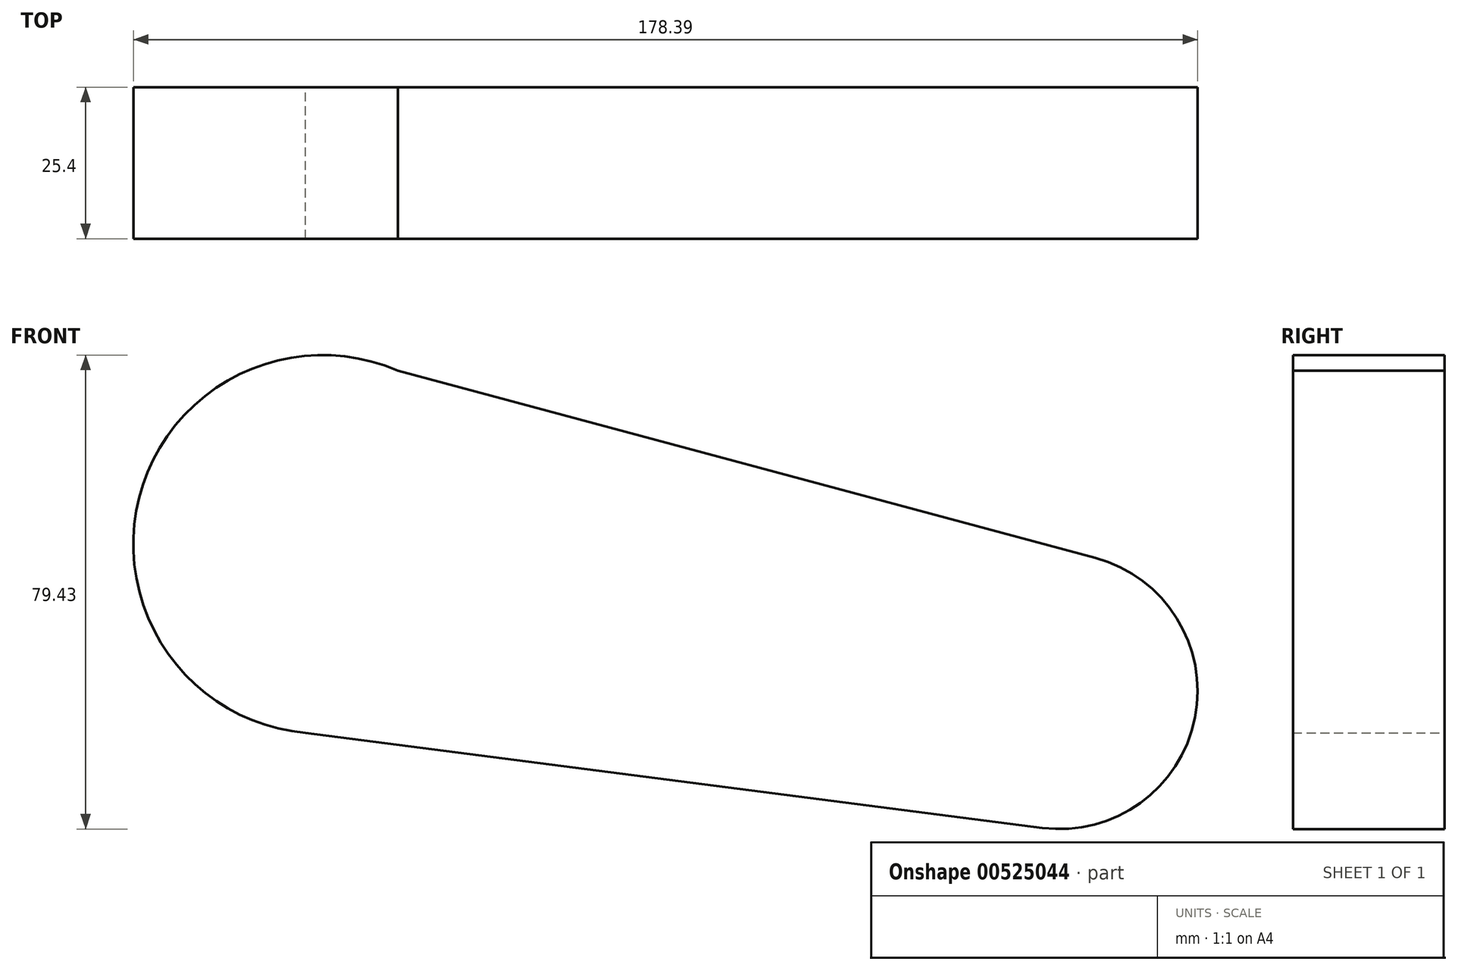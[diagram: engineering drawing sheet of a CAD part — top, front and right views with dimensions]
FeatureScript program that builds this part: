
annotation { "Feature Type Name" : "Feature", "Feature Type Description" : "" }
export const myFeature = defineFeature(function(context is Context, id is Id, definition is map)
    precondition{}
    {
        {
            var Q0;
            Q0=qCreatedBy(makeId("Front.planeOp"),FACE);
            var sketch = newSketch(context, id + "F0", { "sketchPlane" : qUnion([Q0])});
            skCircle(sketch, "E0", {"center": v(-63.37, 39.5) * mm, "radius": 31.73 * mm});
            skCircle(sketch, "E1", {"center": v(60.19, 14.9) * mm, "radius": 23.1 * mm});
            skLineSegment(sketch, "E2", {"start": v(-59.69, 71.02) * mm, "end": v(66.18, 37.22) * mm});
            skLineSegment(sketch, "E3", {"start": v(-66.24, 7.9) * mm, "end": v(57.24, -8.01) * mm});
            skSolve(sketch);
        }
        {
            var Q0;
            Q0=qSketchRegion(id+"F0",true);
            extrude(context, id + "F1", {"entities" : qUnion([Q0]), "depth" : 25.4 * mm, "offsetDistance" : 25.4 * mm});
        }
        {
            var Q0;
            Q0=qSketchRegion(id+"F0",true);
            extrude(context, id + "F2", {"entities" : qUnion([Q0]), "operationType" : NewBodyOperationType.ADD, "depth" : 25.4 * mm, "offsetDistance" : 25.4 * mm});
        }
    });
